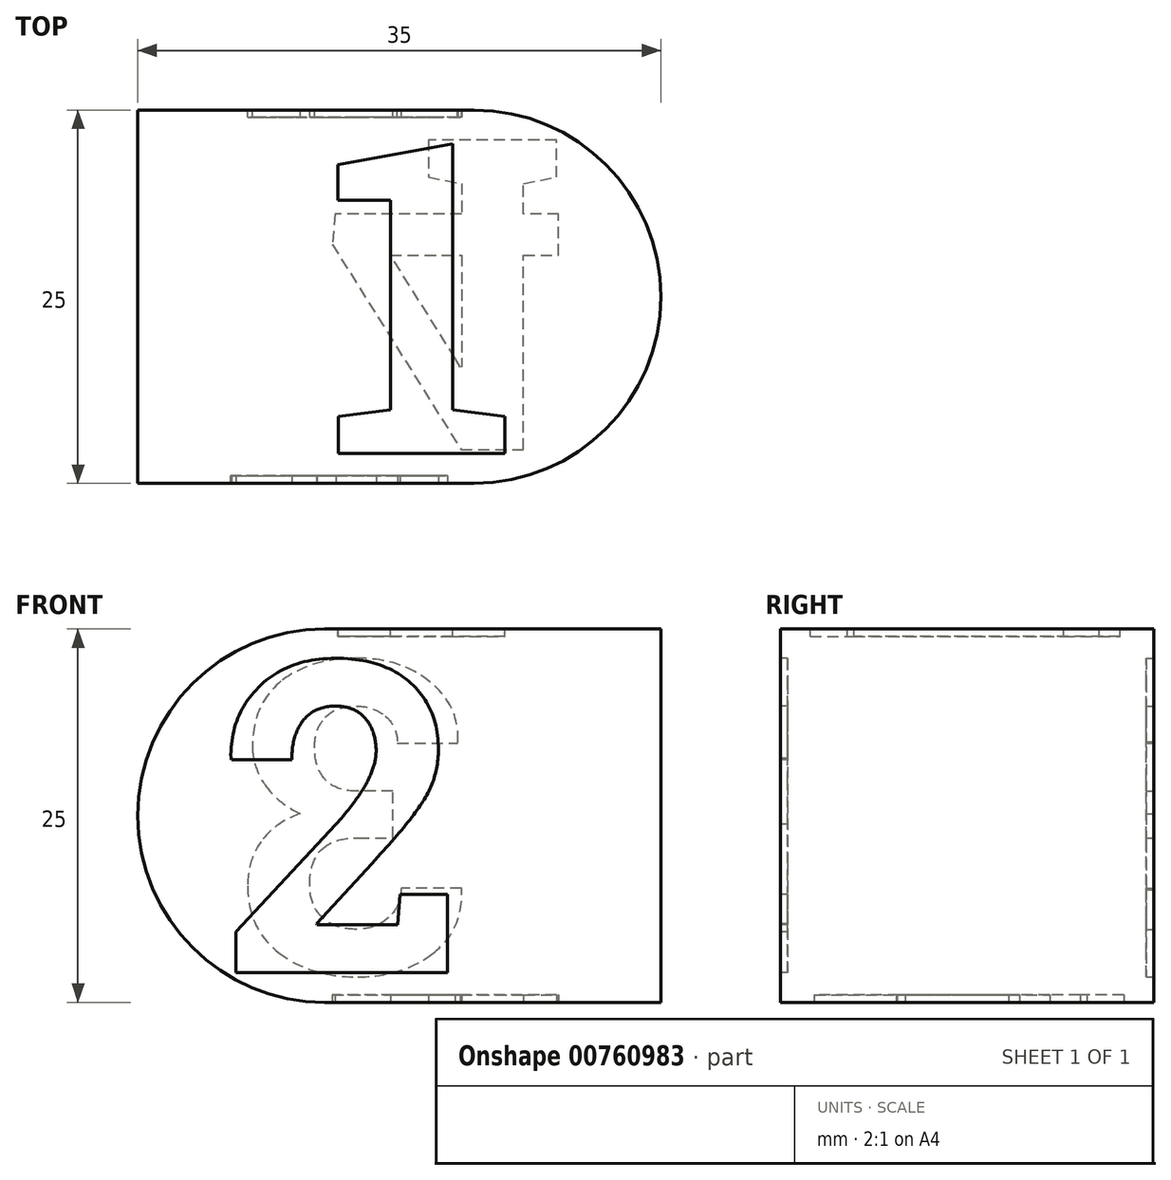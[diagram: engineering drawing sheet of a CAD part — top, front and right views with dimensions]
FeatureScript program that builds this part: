
annotation { "Feature Type Name" : "Feature", "Feature Type Description" : "" }
export const myFeature = defineFeature(function(context is Context, id is Id, definition is map)
    precondition{}
    {
        {
            var Q0;
            Q0=qCreatedBy(makeId("Top.planeOp"),FACE);
            var sketch = newSketch(context, id + "F0", { "sketchPlane" : qUnion([Q0])});
            skLineSegment(sketch, "E0.bottom", {"start": v(0, 0) * mm, "end": v(35, 0) * mm});
            skLineSegment(sketch, "E0.top", {"start": v(0, 25) * mm, "end": v(35, 25) * mm});
            skLineSegment(sketch, "E0.left", {"start": v(0, 0) * mm, "end": v(0, 25) * mm});
            skLineSegment(sketch, "E0.right", {"start": v(35, 0) * mm, "end": v(35, 25) * mm});
            skSolve(sketch);
        }
        {
            var Q0;
            Q0=makeQuery(id+"F0.imprint","IMPRINT",FACE,{"disambiguationData":[TD([[makeQuery(id+"F0.imprint","IMPRINT",EDGE,{"derivedFrom":sQuery(id+"F0.wireOp",EDGE,"E0.bottom")}),1.0]])]});
            extrude(context, id + "F1", {"entities" : qUnion([Q0]), "depth" : 25 * mm});
        }
        {
            var Q0;
            Q0=makeQuery(id+"F1.opExtrude","CAP_EDGE",EDGE,{"disambiguationData":[OSD([sQuery(id+"F0.wireOp",EDGE,"E0.left")])],"isStart":false});
            var Q1;
            Q1=makeQuery(id+"F1.opExtrude","CAP_EDGE",EDGE,{"disambiguationData":[OSD([sQuery(id+"F0.wireOp",EDGE,"E0.left")])],"isStart":true});
            fillet(context, id + "F2", {"entities" : qUnion([Q0, Q1]), "radius" : 12.5 * mm, "tangentPropagation" : true, "allowEdgeOverflow" : false});
        }
        {
            var Q0;
            Q0=makeQuery(id+"F1.opExtrude","SWEPT_EDGE",EDGE,{"disambiguationData":[OSD([sQuery(id+"F0.wireOp",EDGE,"E0.bottom"),sQuery(id+"F0.wireOp",EDGE,"E0.right")])]});
            var Q1;
            Q1=makeQuery(id+"F1.opExtrude","SWEPT_EDGE",EDGE,{"disambiguationData":[OSD([sQuery(id+"F0.wireOp",EDGE,"E0.top"),sQuery(id+"F0.wireOp",EDGE,"E0.right")])]});
            fillet(context, id + "F3", {"entities" : qUnion([Q0, Q1]), "radius" : 12.5 * mm, "tangentPropagation" : true, "allowEdgeOverflow" : false});
        }
        {
            var Q0;
            Q0=makeQuery(id+"F1.opExtrude","CAP_FACE",FACE,{"disambiguationData":[OSD([sQuery(id+"F0.wireOp",EDGE,"E0.bottom"),sQuery(id+"F0.wireOp",EDGE,"E0.top"),sQuery(id+"F0.wireOp",EDGE,"E0.left"),sQuery(id+"F0.wireOp",EDGE,"E0.right")])],"isStart":false});
            var sketch = newSketch(context, id + "F4", { "sketchPlane" : qUnion([Q0])});
            skText(sketch, "E1", { "text": "1", "fontName": "RobotoSlab-Bold.ttf"});
            skLineSegment(sketch, "E2", {"start": v(19.43, 23) * mm, "end": v(19.43, 25) * mm, "construction": true});
            skLineSegment(sketch, "E3", {"start": v(19.43, 2) * mm, "end": v(19.43, 0) * mm, "construction": true});
            const initialGuessF4  = {"E1": [0.0125, 0.002, 1, 0, 0.021]};
            skSetInitialGuess(sketch, initialGuessF4);
            skSolve(sketch);
        }
        {
            var Q0;
            Q0=makeQuery(id+"F1.opExtrude","CAP_FACE",FACE,{"disambiguationData":[OSD([sQuery(id+"F0.wireOp",EDGE,"E0.bottom"),sQuery(id+"F0.wireOp",EDGE,"E0.top"),sQuery(id+"F0.wireOp",EDGE,"E0.left"),sQuery(id+"F0.wireOp",EDGE,"E0.right")])],"isStart":true});
            var sketch = newSketch(context, id + "F5", { "sketchPlane" : qUnion([Q0])});
            skText(sketch, "E4", { "text": "4", "fontName": "RobotoSlab-Bold.ttf"});
            skLineSegment(sketch, "E5", {"start": v(21.23, -2) * mm, "end": v(21.23, 0) * mm, "construction": true});
            skLineSegment(sketch, "E6", {"start": v(21.23, -23) * mm, "end": v(21.23, -25) * mm, "construction": true});
            skPoint(sketch, "E6.endSnap0", {"position": v(17.5, -25) * mm});
            const initialGuessF5  = {"E4": [0.0125, -0.023, 1, 0, 0.021]};
            skSetInitialGuess(sketch, initialGuessF5);
            skSolve(sketch);
        }
        {
            var Q0;
            Q0=makeQuery(id+"F1.opExtrude","SWEPT_FACE",FACE,{"disambiguationData":[OSD([sQuery(id+"F0.wireOp",EDGE,"E0.bottom")])]});
            var sketch = newSketch(context, id + "F6", { "sketchPlane" : qUnion([Q0])});
            skText(sketch, "E7", { "text": "2", "fontName": "RobotoSlab-Bold.ttf"});
            skLineSegment(sketch, "E8", {"start": v(14, 23) * mm, "end": v(14, 25) * mm, "construction": true});
            skLineSegment(sketch, "E9", {"start": v(14, 2) * mm, "end": v(14, 0) * mm, "construction": true});
            const initialGuessF6  = {"E7": [0.00552, 0.002, 1, 0, 0.021]};
            skSetInitialGuess(sketch, initialGuessF6);
            skSolve(sketch);
        }
        {
            var Q0;
            Q0=makeQuery(id+"F1.opExtrude","SWEPT_FACE",FACE,{"disambiguationData":[OSD([sQuery(id+"F0.wireOp",EDGE,"E0.top")])]});
            var sketch = newSketch(context, id + "F7", { "sketchPlane" : qUnion([Q0])});
            skText(sketch, "E10", { "text": "3", "fontName": "RobotoSlab-Bold.ttf"});
            skLineSegment(sketch, "E11", {"start": v(-14.03, 2) * mm, "end": v(-14.03, 0) * mm, "construction": true});
            skLineSegment(sketch, "E12", {"start": v(-14.03, 23) * mm, "end": v(-14.03, 25) * mm, "construction": true});
            const initialGuessF7  = {"E10": [-0.0225, 0.002, 1, 0, 0.021]};
            skSetInitialGuess(sketch, initialGuessF7);
            skSolve(sketch);
        }
        {
            var Q0;
            Q0=qSketchRegion(id+"F4",true);
            extrude(context, id + "F8", {"entities" : qUnion([Q0]), "operationType" : NewBodyOperationType.REMOVE, "oppositeDirection" : true, "depth" : .5 * mm});
        }
        {
            var Q0;
            Q0=qSketchRegion(id+"F5",true);
            extrude(context, id + "F9", {"entities" : qUnion([Q0]), "operationType" : NewBodyOperationType.REMOVE, "oppositeDirection" : true, "depth" : .5 * mm});
        }
        {
            var Q0;
            Q0=qSketchRegion(id+"F6",true);
            extrude(context, id + "F10", {"entities" : qUnion([Q0]), "operationType" : NewBodyOperationType.REMOVE, "oppositeDirection" : true, "depth" : .5 * mm});
        }
        {
            var Q0;
            Q0=qSketchRegion(id+"F7",true);
            extrude(context, id + "F11", {"entities" : qUnion([Q0]), "operationType" : NewBodyOperationType.REMOVE, "oppositeDirection" : true, "depth" : .5 * mm});
        }
    });
